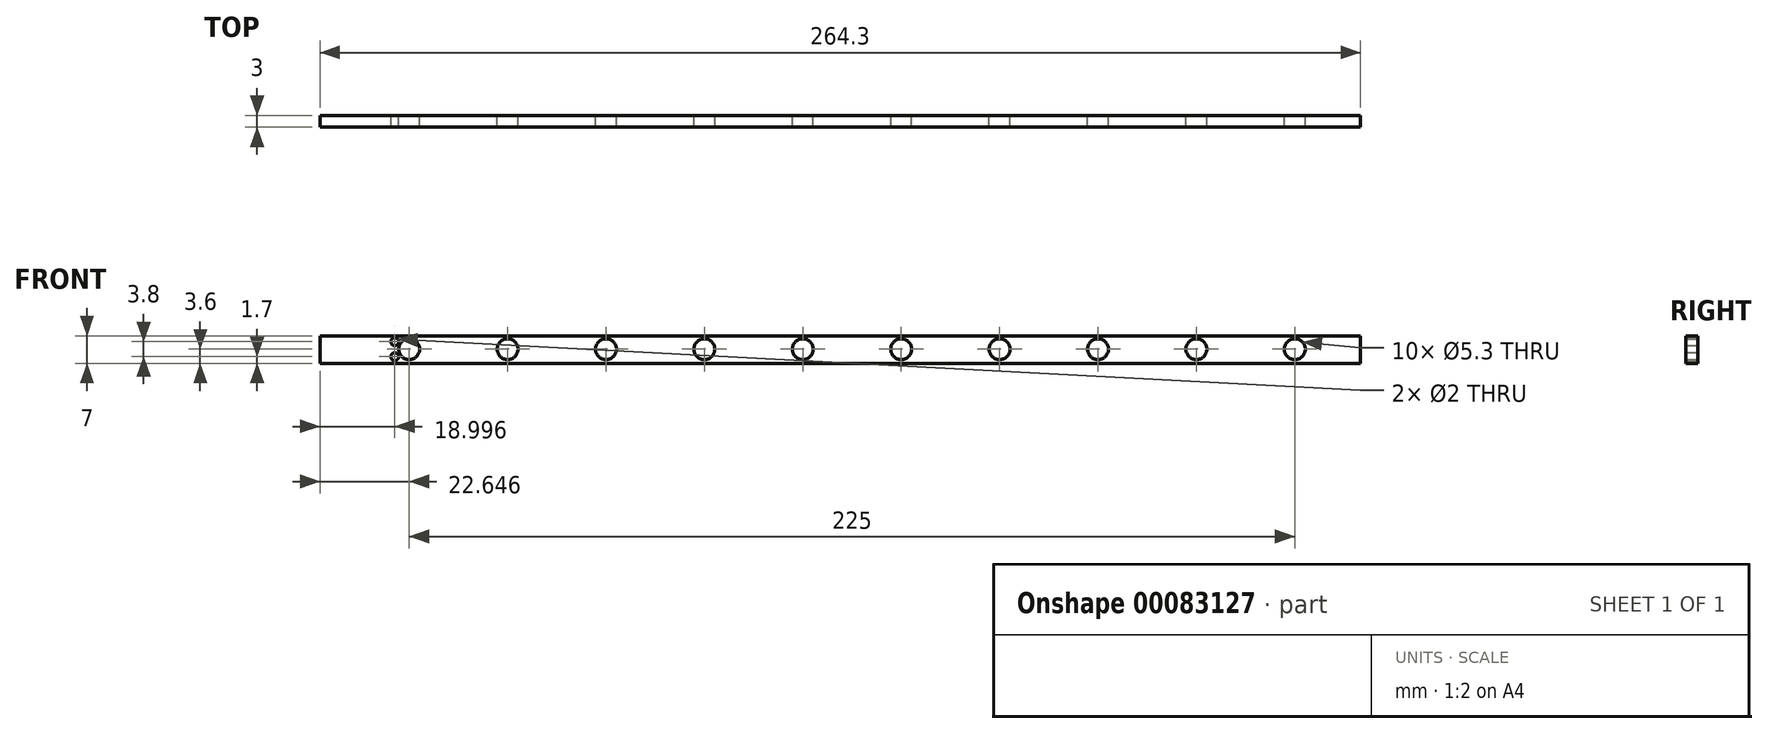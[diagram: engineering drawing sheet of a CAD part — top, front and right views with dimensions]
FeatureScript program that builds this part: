
annotation { "Feature Type Name" : "Feature", "Feature Type Description" : "" }
export const myFeature = defineFeature(function(context is Context, id is Id, definition is map)
    precondition{}
    {
        {
            var Q0;
            Q0=qCreatedBy(makeId("Front.planeOp"),FACE);
            var sketch = newSketch(context, id + "F0", { "sketchPlane" : qUnion([Q0])});
            skLineSegment(sketch, "E0.bottom", {"start": v(-115.84, 3.4) * mm, "end": v(148.46, 3.4) * mm});
            skLineSegment(sketch, "E0.top", {"start": v(-115.84, -3.6) * mm, "end": v(148.46, -3.6) * mm});
            skLineSegment(sketch, "E0.left", {"start": v(-115.84, 3.4) * mm, "end": v(-115.84, -3.6) * mm});
            skLineSegment(sketch, "E0.right", {"start": v(148.46, 3.4) * mm, "end": v(148.46, -3.6) * mm});
            skPoint(sketch, "E0.middle", {"position": v(16.3, -0.1) * mm});
            skCircle(sketch, "E1", {"center": v(-93.2, 0) * mm, "radius": 2.65 * mm});
            skCircle(sketch, "E2.1.0.0", {"center": v(-68.2, 0) * mm, "radius": 2.65 * mm});
            skCircle(sketch, "E2.2.0.0", {"center": v(-43.2, 0) * mm, "radius": 2.65 * mm});
            skCircle(sketch, "E2.3.0.0", {"center": v(-18.2, 0) * mm, "radius": 2.65 * mm});
            skCircle(sketch, "E2.4.0.0", {"center": v(6.8, 0) * mm, "radius": 2.65 * mm});
            skCircle(sketch, "E2.5.0.0", {"center": v(31.8, 0) * mm, "radius": 2.65 * mm});
            skCircle(sketch, "E2.6.0.0", {"center": v(56.8, 0) * mm, "radius": 2.65 * mm});
            skCircle(sketch, "E2.7.0.0", {"center": v(81.8, 0) * mm, "radius": 2.65 * mm});
            skCircle(sketch, "E2.8.0.0", {"center": v(106.8, 0) * mm, "radius": 2.65 * mm});
            skCircle(sketch, "E2.9.0.0", {"center": v(131.8, 0) * mm, "radius": 2.65 * mm});
            skLineSegment(sketch, "E2.direction1", {"start": v(-93.2, 0) * mm, "end": v(-68.2, 0) * mm, "construction": true});
            skCircle(sketch, "E3", {"center": v(-96.84, 1.9) * mm, "radius": 1 * mm});
            skCircle(sketch, "E4.MirrorC", {"center": v(-96.84, -1.9) * mm, "radius": 1 * mm});
            skSolve(sketch);
        }
        {
            var Q0;
            Q0 = qSketchRegion(id + "F0", true);
            extrude(context, id + "F1", {"entities" : qUnion([Q0]), "depth" : 3 * mm});
        }
    });
